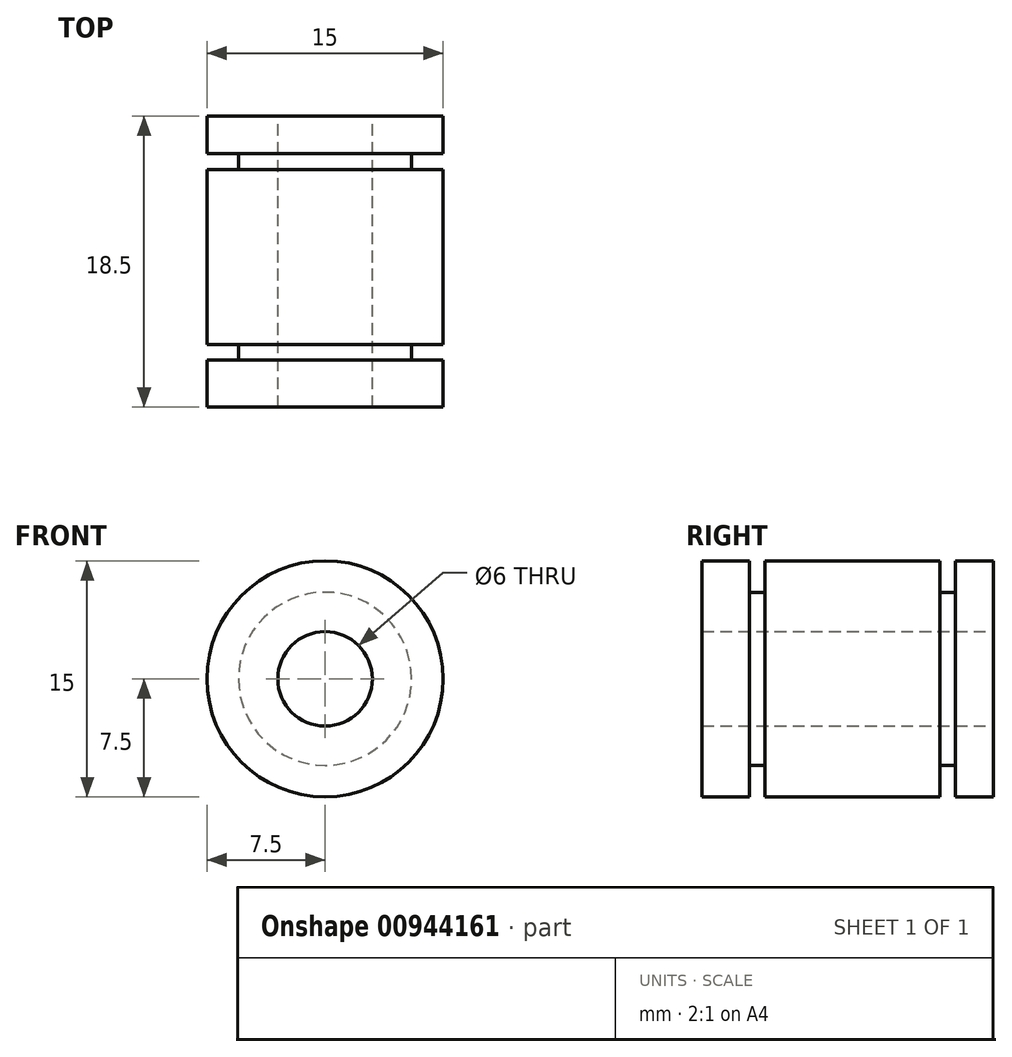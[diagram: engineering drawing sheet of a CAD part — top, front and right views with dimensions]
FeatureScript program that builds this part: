
annotation { "Feature Type Name" : "Feature", "Feature Type Description" : "" }
export const myFeature = defineFeature(function(context is Context, id is Id, definition is map)
    precondition{}
    {
        {
            var Q0;
            Q0=qCreatedBy(makeId("Front.planeOp"),FACE);
            var sketch = newSketch(context, id + "F0", { "sketchPlane" : qUnion([Q0])});
            skCircle(sketch, "E0", {"center": v(0, 0) * mm, "radius": 7.5 * mm});
            skCircle(sketch, "E1", {"center": v(0, 0) * mm, "radius": 3 * mm});
            skSolve(sketch);
        }
        {
            var Q0;
            Q0=qSketchRegion(id+"F0",true);
            extrude(context, id + "F1", {"entities" : qUnion([Q0]), "depth" : 2.4 * mm, "offsetDistance" : 25 * mm});
        }
        {
            var Q0;
            Q0=makeQuery(id+"F1.opExtrude","CAP_FACE",FACE,{"disambiguationData":[OSD([sQuery(id+"F0.wireOp",EDGE,"E0"),sQuery(id+"F0.wireOp",EDGE,"E1")])],"isStart":false});
            var sketch = newSketch(context, id + "F2", { "sketchPlane" : qUnion([Q0])});
            skCircle(sketch, "E2", {"center": v(0, 0) * mm, "radius": 5.5 * mm});
            skSolve(sketch);
        }
        {
            var Q0;
            Q0=makeQuery(id+"F2.imprint","IMPRINT",FACE,{"disambiguationData":[TD([[makeQuery(id+"F2.imprint","IMPRINT",EDGE,{"derivedFrom":sQuery(id+"F2.wireOp",EDGE,"E2")}),1.0]])]});
            extrude(context, id + "F3", {"entities" : qUnion([Q0]), "operationType" : NewBodyOperationType.ADD, "depth" : 1 * mm});
        }
        {
            var Q0;
            Q0=makeQuery(id+"F3.opExtrude","CAP_FACE",FACE,{"disambiguationData":[OSD([sQuery(id+"F0.wireOp",EDGE,"E1"),sQuery(id+"F2.wireOp",EDGE,"E2")])],"isStart":false});
            var sketch = newSketch(context, id + "F4", { "sketchPlane" : qUnion([Q0])});
            skCircle(sketch, "E3.0", {"center": v(0, 0) * mm, "radius": 7.5 * mm});
            skSolve(sketch);
        }
        {
            var Q0;
            Q0=makeQuery(id+"F4.imprint","IMPRINT",FACE,{"disambiguationData":[TD([[makeQuery(id+"F4.imprint","IMPRINT",EDGE,{"derivedFrom":makeQuery(id+"F3.opExtrude","CAP_EDGE",EDGE,{"disambiguationData":[OSD([sQuery(id+"F2.wireOp",EDGE,"E2")])],"isStart":false})}),1.0]])]});
            var Q1;
            Q1=makeQuery(id+"F4.imprint","IMPRINT",FACE,{"disambiguationData":[TD([[makeQuery(id+"F4.imprint","IMPRINT",EDGE,{"derivedFrom":sQuery(id+"F4.wireOp",EDGE,"E3.0")}),1.0]])]});
            extrude(context, id + "F5", {"entities" : qUnion([Q0, Q1]), "operationType" : NewBodyOperationType.ADD, "depth" : 11.1 * mm});
        }
        {
            var Q0;
            Q0=makeQuery(id+"F5.opExtrude","CAP_FACE",FACE,{"disambiguationData":[OSD([sQuery(id+"F0.wireOp",EDGE,"E1"),sQuery(id+"F4.wireOp",EDGE,"E3.0")])],"isStart":false});
            var sketch = newSketch(context, id + "F6", { "sketchPlane" : qUnion([Q0])});
            skCircle(sketch, "E4.0", {"center": v(0, 0) * mm, "radius": 5.5 * mm});
            skSolve(sketch);
        }
        {
            var Q0;
            Q0=makeQuery(id+"F6.imprint","IMPRINT",FACE,{"disambiguationData":[TD([[makeQuery(id+"F6.imprint","IMPRINT",EDGE,{"derivedFrom":sQuery(id+"F6.wireOp",EDGE,"E4.0")}),1.0]])]});
            extrude(context, id + "F7", {"entities" : qUnion([Q0]), "operationType" : NewBodyOperationType.ADD, "depth" : 1 * mm});
        }
        {
            var Q0;
            Q0=makeQuery(id+"F7.opExtrude","CAP_FACE",FACE,{"disambiguationData":[OSD([sQuery(id+"F0.wireOp",EDGE,"E1"),sQuery(id+"F6.wireOp",EDGE,"E4.0")])],"isStart":false});
            var sketch = newSketch(context, id + "F8", { "sketchPlane" : qUnion([Q0])});
            skCircle(sketch, "E5.0", {"center": v(0, 0) * mm, "radius": 7.5 * mm});
            skSolve(sketch);
        }
        {
            var Q0;
            Q0=makeQuery(id+"F8.imprint","IMPRINT",FACE,{"disambiguationData":[TD([[makeQuery(id+"F8.imprint","IMPRINT",EDGE,{"derivedFrom":sQuery(id+"F8.wireOp",EDGE,"E5.0")}),1.0]])]});
            var Q1;
            Q1=makeQuery(id+"F8.imprint","IMPRINT",FACE,{"disambiguationData":[TD([[makeQuery(id+"F8.imprint","IMPRINT",EDGE,{"derivedFrom":makeQuery(id+"F7.opExtrude","CAP_EDGE",EDGE,{"disambiguationData":[OSD([sQuery(id+"F6.wireOp",EDGE,"E4.0")])],"isStart":false})}),1.0]])]});
            extrude(context, id + "F9", {"entities" : qUnion([Q0, Q1]), "operationType" : NewBodyOperationType.ADD, "depth" : 3 * mm});
        }
    });
